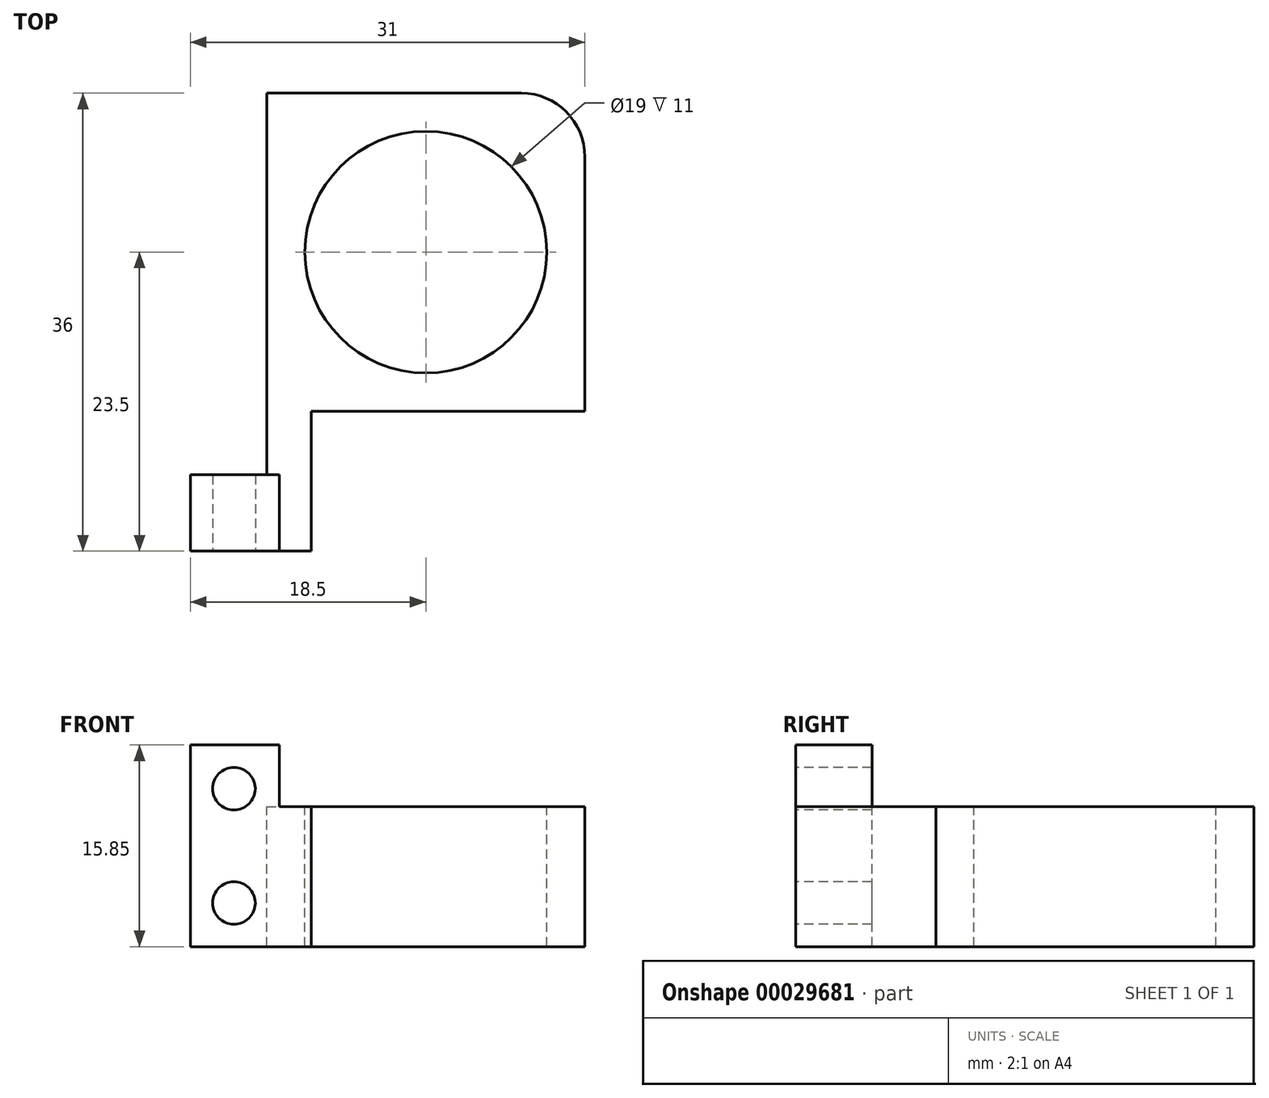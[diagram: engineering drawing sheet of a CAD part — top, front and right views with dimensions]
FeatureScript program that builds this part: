
annotation { "Feature Type Name" : "Feature", "Feature Type Description" : "" }
export const myFeature = defineFeature(function(context is Context, id is Id, definition is map)
    precondition{}
    {
        {
            var Q0;
            Q0=qCreatedBy(makeId("Top.planeOp"),FACE);
            var sketch = newSketch(context, id + "F0", { "sketchPlane" : qUnion([Q0])});
            skLineSegment(sketch, "E0.bottom", {"start": v(0, 0) * mm, "end": v(31, 0) * mm});
            skLineSegment(sketch, "E0.top", {"start": v(0, 36) * mm, "end": v(31, 36) * mm});
            skLineSegment(sketch, "E0.left", {"start": v(0, 0) * mm, "end": v(0, 36) * mm});
            skLineSegment(sketch, "E0.right", {"start": v(31, 0) * mm, "end": v(31, 36) * mm});
            skSolve(sketch);
        }
        {
            var Q0;
            Q0=qSketchRegion(id+"F0",true);
            extrude(context, id + "F1", {"entities" : qUnion([Q0]), "depth" : 11 * mm});
        }
        {
            var Q0;
            Q0=makeQuery(id+"F1.opExtrude","CAP_FACE",FACE,{"disambiguationData":[OSD([sQuery(id+"F0.wireOp",EDGE,"E0.bottom"),sQuery(id+"F0.wireOp",EDGE,"E0.top"),sQuery(id+"F0.wireOp",EDGE,"E0.left"),sQuery(id+"F0.wireOp",EDGE,"E0.right")])],"isStart":false});
            var sketch = newSketch(context, id + "F2", { "sketchPlane" : qUnion([Q0])});
            skCircle(sketch, "E1", {"center": v(18.5, 23.5) * mm, "radius": 9.5 * mm});
            skLineSegment(sketch, "E2.bottom", {"start": v(0, 36) * mm, "end": v(6, 36) * mm});
            skLineSegment(sketch, "E2.top", {"start": v(0, 6) * mm, "end": v(6, 6) * mm});
            skLineSegment(sketch, "E2.left", {"start": v(0, 36) * mm, "end": v(0, 6) * mm});
            skLineSegment(sketch, "E2.right", {"start": v(6, 36) * mm, "end": v(6, 6) * mm});
            skLineSegment(sketch, "E3.bottom", {"start": v(31, 0) * mm, "end": v(9.5, 0) * mm});
            skLineSegment(sketch, "E3.top", {"start": v(31, 11) * mm, "end": v(9.5, 11) * mm});
            skLineSegment(sketch, "E3.left", {"start": v(31, 0) * mm, "end": v(31, 11) * mm});
            skLineSegment(sketch, "E3.right", {"start": v(9.5, 0) * mm, "end": v(9.5, 11) * mm});
            skSolve(sketch);
        }
        {
            var Q0;
            Q0=qSketchRegion(id+"F2",true);
            extrude(context, id + "F3", {"entities" : qUnion([Q0]), "operationType" : NewBodyOperationType.REMOVE, "oppositeDirection" : true, "depth" : 25 * mm});
        }
        {
            var Q0;
            Q0=makeQuery(id+"F1.opExtrude","CAP_FACE",FACE,{"disambiguationData":[OSD([sQuery(id+"F0.wireOp",EDGE,"E0.bottom"),sQuery(id+"F0.wireOp",EDGE,"E0.top"),sQuery(id+"F0.wireOp",EDGE,"E0.left"),sQuery(id+"F0.wireOp",EDGE,"E0.right")])],"isStart":false});
            var sketch = newSketch(context, id + "F4", { "sketchPlane" : qUnion([Q0])});
            skLineSegment(sketch, "E4.bottom", {"start": v(0, 0) * mm, "end": v(7, 0) * mm});
            skLineSegment(sketch, "E4.top", {"start": v(0, 6) * mm, "end": v(7, 6) * mm});
            skLineSegment(sketch, "E4.left", {"start": v(0, 0) * mm, "end": v(0, 6) * mm});
            skLineSegment(sketch, "E4.right", {"start": v(7, 0) * mm, "end": v(7, 6) * mm});
            skSolve(sketch);
        }
        {
            var Q0;
            Q0=makeQuery(id+"F4.imprint","IMPRINT",FACE,{"disambiguationData":[TD([[makeQuery(id+"F4.imprint","IMPRINT",EDGE,{"derivedFrom":sQuery(id+"F4.wireOp",EDGE,"E4.bottom")}),1.0]])]});
            extrude(context, id + "F5", {"entities" : qUnion([Q0]), "operationType" : NewBodyOperationType.ADD, "depth" : 4.85 * mm});
        }
        {
            var Q0;
            Q0=makeQuery(id+"F5.boolean.opBoolean","MERGE",FACE,{"derivedFrom":[makeQuery(id+"F1.opExtrude","SWEPT_FACE",FACE,{"disambiguationData":[OSD([sQuery(id+"F0.wireOp",EDGE,"E0.bottom")])]}),makeQuery(id+"F5.opExtrude","SWEPT_FACE",FACE,{"disambiguationData":[OSD([sQuery(id+"F4.wireOp",EDGE,"a4e6f074-5849-4971-a416-d7e5f2b247c1.top")])]})]});
            var sketch = newSketch(context, id + "F6", { "sketchPlane" : qUnion([Q0])});
            skCircle(sketch, "E5", {"center": v(3.42, 12.43) * mm, "radius": 1.67 * mm});
            skCircle(sketch, "E6", {"center": v(3.43, 3.43) * mm, "radius": 1.68 * mm});
            skSolve(sketch);
        }
        {
            var Q0;
            Q0=qSketchRegion(id+"F6",true);
            extrude(context, id + "F7", {"entities" : qUnion([Q0]), "operationType" : NewBodyOperationType.REMOVE, "oppositeDirection" : true, "depth" : 25 * mm});
        }
        {
            var Q0;
            Q0=makeQuery(id+"F1.opExtrude","SWEPT_EDGE",EDGE,{"disambiguationData":[OSD([sQuery(id+"F0.wireOp",EDGE,"E0.bottom"),sQuery(id+"F0.wireOp",EDGE,"E0.right")])]});
            var Q1;
            Q1=makeQuery(id+"F1.opExtrude","SWEPT_EDGE",EDGE,{"disambiguationData":[OSD([sQuery(id+"F0.wireOp",EDGE,"E0.top"),sQuery(id+"F0.wireOp",EDGE,"E0.right")])]});
            var Q2;
            Q2=makeQuery(id+"F3.boolean.opBoolean","COPY",EDGE,{"derivedFrom":makeQuery(id+"F3.opExtrude","SWEPT_EDGE",EDGE,{"disambiguationData":[OSD([sQuery(id+"F0.wireOp",EDGE,"E0.top"),sQuery(id+"F2.wireOp",EDGE,"E2.bottom"),sQuery(id+"F2.wireOp",EDGE,"E2.right")])]})});
            var Q3;
            Q3=makeQuery(id+"F3.boolean.opBoolean","COPY",EDGE,{"derivedFrom":makeQuery(id+"F3.opExtrude","SWEPT_EDGE",EDGE,{"disambiguationData":[OSD([sQuery(id+"F0.wireOp",EDGE,"E0.right"),sQuery(id+"F2.wireOp",EDGE,"E3.top"),sQuery(id+"F2.wireOp",EDGE,"E3.left")])]})});
            fillet(context, id + "F8", {"entities" : qUnion([Q0, Q1, Q2, Q3]), "radius" : 5 * mm, "tangentPropagation" : true, "allowEdgeOverflow" : false});
        }
    });
